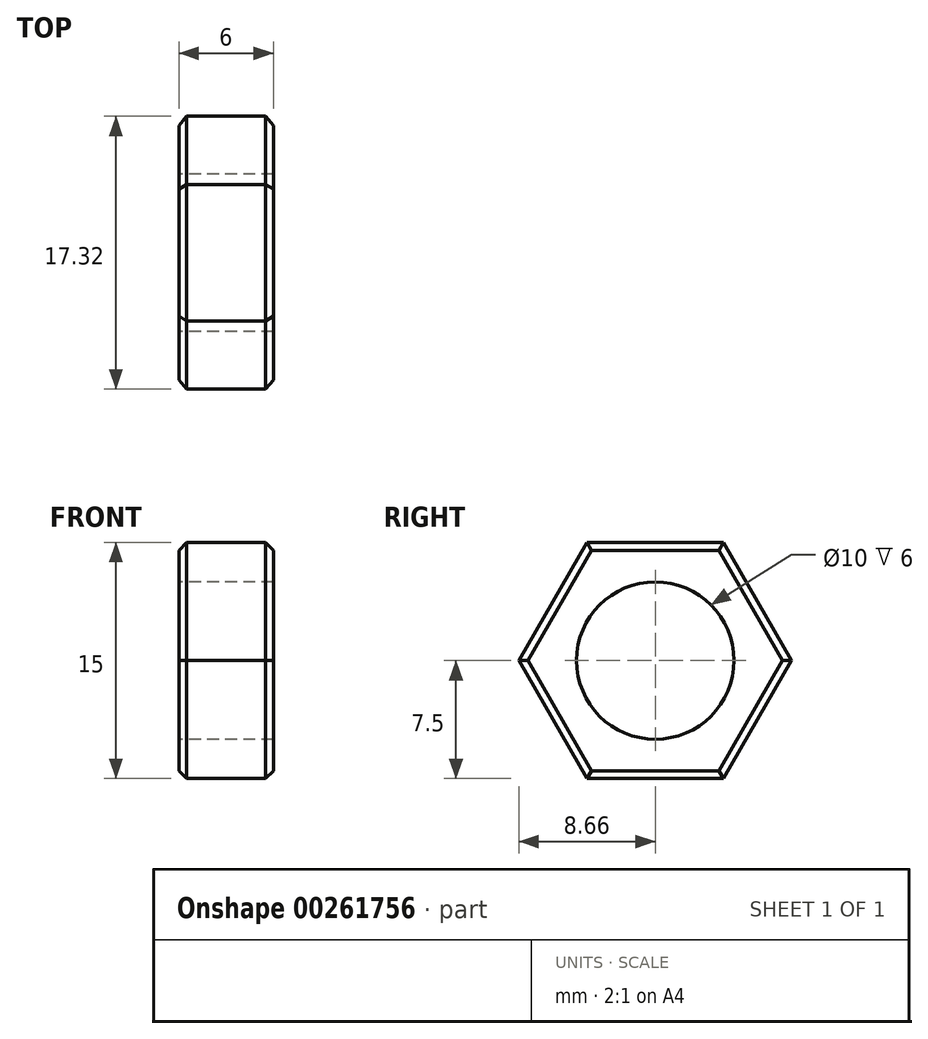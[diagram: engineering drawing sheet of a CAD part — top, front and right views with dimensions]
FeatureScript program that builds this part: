
annotation { "Feature Type Name" : "Feature", "Feature Type Description" : "" }
export const myFeature = defineFeature(function(context is Context, id is Id, definition is map)
    precondition{}
    {
        {
            var Q0;
            Q0=qCreatedBy(makeId("Right.planeOp"),FACE);
            var sketch = newSketch(context, id + "F0", { "sketchPlane" : qUnion([Q0])});
            skCircle(sketch, "E0.cCircle", {"center": v(0, 0) * mm, "radius": 7.5 * mm, "construction": true});
            skLineSegment(sketch, "E0.0", {"start": v(-4.33, 7.5) * mm, "end": v(4.33, 7.5) * mm});
            skLineSegment(sketch, "E0.1", {"start": v(4.33, 7.5) * mm, "end": v(8.66, 0) * mm});
            skLineSegment(sketch, "E0.2", {"start": v(8.66, 0) * mm, "end": v(4.33, -7.5) * mm});
            skLineSegment(sketch, "E0.3", {"start": v(4.33, -7.5) * mm, "end": v(-4.33, -7.5) * mm});
            skLineSegment(sketch, "E0.4", {"start": v(-4.33, -7.5) * mm, "end": v(-8.66, 0) * mm});
            skLineSegment(sketch, "E0.5", {"start": v(-8.66, 0) * mm, "end": v(-4.33, 7.5) * mm});
            skPoint(sketch, "E0.0.midPoint", {"position": v(0, 7.5) * mm});
            skCircle(sketch, "E1", {"center": v(0, 0) * mm, "radius": 5 * mm});
            skSolve(sketch);
        }
        {
            var Q0;
            Q0 = qSketchRegion(id + "F0", true);
            extrude(context, id + "F1", {"entities" : qUnion([Q0]), "depth" : 6 * mm});
        }
        {
            var Q0;
            Q0=makeQuery(id+"F1.opExtrude","CAP_EDGE",EDGE,{"disambiguationData":[OSD([sQuery(id+"F0.wireOp",EDGE,"E0.0")])],"isStart":false});
            var Q1;
            Q1=makeQuery(id+"F1.opExtrude","CAP_EDGE",EDGE,{"disambiguationData":[OSD([sQuery(id+"F0.wireOp",EDGE,"E0.1")])],"isStart":false});
            var Q2;
            Q2=makeQuery(id+"F1.opExtrude","CAP_EDGE",EDGE,{"disambiguationData":[OSD([sQuery(id+"F0.wireOp",EDGE,"E0.2")])],"isStart":false});
            var Q3;
            Q3=makeQuery(id+"F1.opExtrude","CAP_EDGE",EDGE,{"disambiguationData":[OSD([sQuery(id+"F0.wireOp",EDGE,"E0.3")])],"isStart":false});
            var Q4;
            Q4=makeQuery(id+"F1.opExtrude","CAP_EDGE",EDGE,{"disambiguationData":[OSD([sQuery(id+"F0.wireOp",EDGE,"E0.5")])],"isStart":false});
            var Q5;
            Q5=makeQuery(id+"F1.opExtrude","CAP_EDGE",EDGE,{"disambiguationData":[OSD([sQuery(id+"F0.wireOp",EDGE,"E0.1")])],"isStart":true});
            var Q6;
            Q6=makeQuery(id+"F1.opExtrude","CAP_EDGE",EDGE,{"disambiguationData":[OSD([sQuery(id+"F0.wireOp",EDGE,"E0.0")])],"isStart":true});
            var Q7;
            Q7=makeQuery(id+"F1.opExtrude","CAP_EDGE",EDGE,{"disambiguationData":[OSD([sQuery(id+"F0.wireOp",EDGE,"E0.2")])],"isStart":true});
            var Q8;
            Q8=makeQuery(id+"F1.opExtrude","CAP_EDGE",EDGE,{"disambiguationData":[OSD([sQuery(id+"F0.wireOp",EDGE,"E0.3")])],"isStart":true});
            var Q9;
            Q9=makeQuery(id+"F1.opExtrude","CAP_EDGE",EDGE,{"disambiguationData":[OSD([sQuery(id+"F0.wireOp",EDGE,"E0.4")])],"isStart":true});
            var Q10;
            Q10=makeQuery(id+"F1.opExtrude","CAP_EDGE",EDGE,{"disambiguationData":[OSD([sQuery(id+"F0.wireOp",EDGE,"E0.5")])],"isStart":true});
            var Q11;
            Q11=makeQuery(id+"F1.opExtrude","CAP_EDGE",EDGE,{"disambiguationData":[OSD([sQuery(id+"F0.wireOp",EDGE,"E0.4")])],"isStart":false});
            chamfer(context, id + "F2", {"entities" : qUnion([Q0, Q1, Q2, Q3, Q4, Q5, Q6, Q7, Q8, Q9, Q10, Q11]), "width" : 0.5 * mm, "tangentPropagation" : true});
        }
    });
